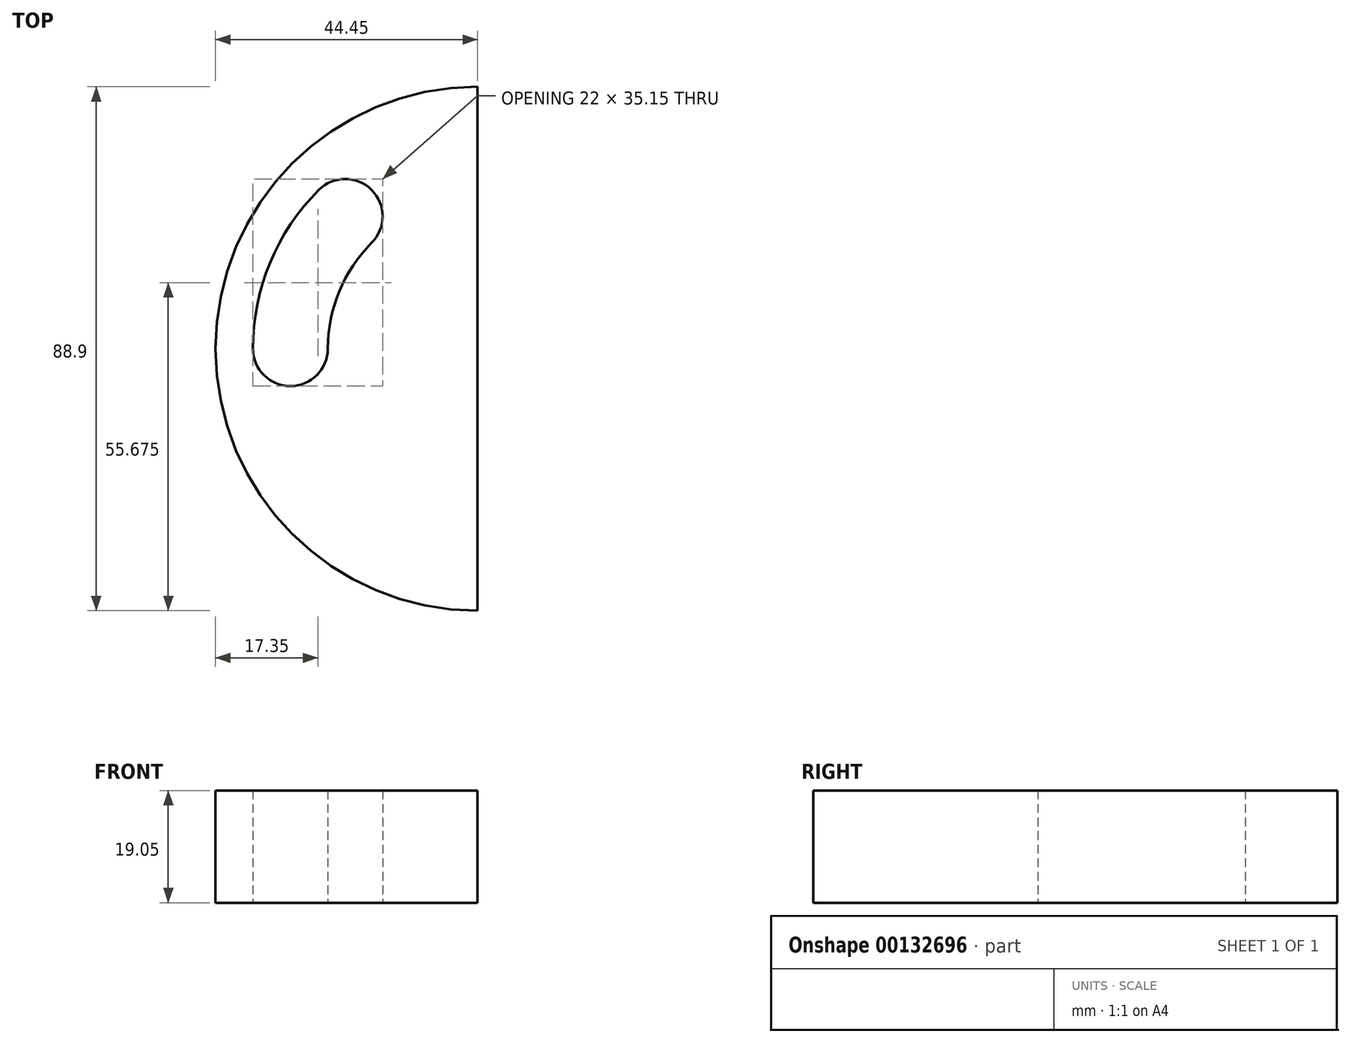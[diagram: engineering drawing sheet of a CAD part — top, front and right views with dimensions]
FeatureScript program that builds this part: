
annotation { "Feature Type Name" : "Feature", "Feature Type Description" : "" }
export const myFeature = defineFeature(function(context is Context, id is Id, definition is map)
    precondition{}
    {
        {
            var Q0;
            Q0=qCreatedBy(makeId("Top.planeOp"),FACE);
            var sketch = newSketch(context, id + "F0", { "sketchPlane" : qUnion([Q0])});
            skCircle(sketch, "E0", {"center": v(0, 0) * mm, "radius": 44.45 * mm});
            skLineSegment(sketch, "E1", {"start": v(0, 72.68) * mm, "end": v(0, -70.78) * mm});
            skLineSegment(sketch, "E2", {"start": v(70.46, 0) * mm, "end": v(34.93, 0) * mm});
            skLineSegment(sketch, "E3.trimOffspring", {"start": v(-38.1, 0) * mm, "end": v(-64.18, 0) * mm});
            skArc(sketch, "E4.MirrorC", {"start": v(28.57, 0) * mm, "mid": v(31.75, 3.17) * mm, "end": v(34.92, 0) * mm});
            skArc(sketch, "E5.MirrorC", {"start": v(-17.96, 17.96) * mm, "mid": v(-17.96, 26.94) * mm, "end": v(-26.94, 26.94) * mm});
            skArc(sketch, "E6.MirrorC", {"start": v(23.54, -16.2) * mm, "mid": v(18.37, -27.31) * mm, "end": v(28.42, -20.3) * mm});
            skArc(sketch, "E7.trimOffspring", {"start": v(28.42, -20.3) * mm, "mid": v(33.26, -10.66) * mm, "end": v(34.92, 0) * mm});
            skArc(sketch, "E8.trimOffspring", {"start": v(23.54, -16.2) * mm, "mid": v(27.29, -8.48) * mm, "end": v(28.57, 0) * mm});
            skArc(sketch, "E9", {"start": v(0, -25.4) * mm, "mid": v(25.4, 0) * mm, "end": v(0, 25.4) * mm});
            skArc(sketch, "E10", {"start": v(0, -38.1) * mm, "mid": v(38.1, 0) * mm, "end": v(0, 38.1) * mm});
            skArc(sketch, "E11", {"start": v(-38.1, 0) * mm, "mid": v(-31.75, -6.35) * mm, "end": v(-25.4, 0) * mm});
            skArc(sketch, "E12.trimOffspring", {"start": v(-17.96, 17.96) * mm, "mid": v(-23.47, 9.72) * mm, "end": v(-25.4, 0) * mm});
            skArc(sketch, "E13.trimOffspring", {"start": v(-26.94, 26.94) * mm, "mid": v(-35.2, 14.58) * mm, "end": v(-38.1, 0) * mm});
            skSolve(sketch);
        }
        {
            var Q0;
            Q0=makeQuery(id+"F0.imprint","IMPRINT",FACE,{"disambiguationData":[TD([[makeQuery(id+"F0.imprint","IMPRINT",EDGE,{"derivedFrom":sQuery(id+"F0.wireOp",EDGE,"E5.MirrorC")}),-1.0]])]});
            extrude(context, id + "F1", {"entities" : qUnion([Q0]), "depth" : 19.05 * mm});
        }
    });
